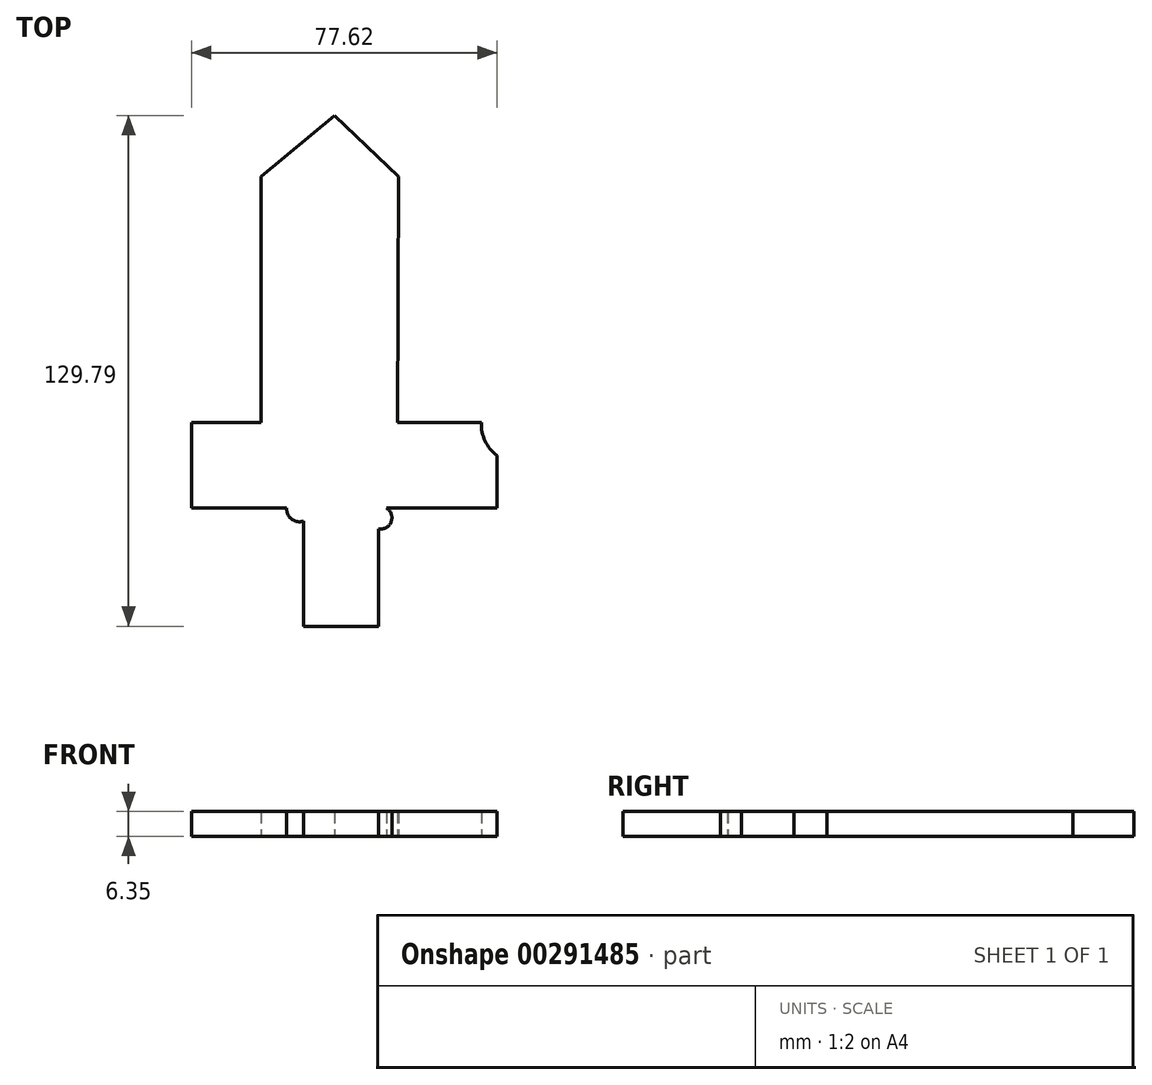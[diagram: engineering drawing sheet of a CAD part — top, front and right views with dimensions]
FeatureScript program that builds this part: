
annotation { "Feature Type Name" : "Feature", "Feature Type Description" : "" }
export const myFeature = defineFeature(function(context is Context, id is Id, definition is map)
    precondition{}
    {
        {
            var Q0;
            Q0=qCreatedBy(makeId("Top.planeOp"),FACE);
            var sketch = newSketch(context, id + "F0", { "sketchPlane" : qUnion([Q0])});
            skLineSegment(sketch, "E0", {"start": v(-7.85, -13.36) * mm, "end": v(-7.87, -43.45) * mm});
            skLineSegment(sketch, "E1", {"start": v(-7.87, -43.45) * mm, "end": v(11.29, -43.45) * mm});
            skLineSegment(sketch, "E2", {"start": v(11.29, -43.45) * mm, "end": v(11.29, -13.36) * mm});
            skLineSegment(sketch, "E3", {"start": v(11.29, -13.36) * mm, "end": v(41.34, -13.36) * mm});
            skLineSegment(sketch, "E4", {"start": v(41.34, 8.3) * mm, "end": v(37.36, 8.3) * mm});
            skLineSegment(sketch, "E5", {"start": v(-31.7, 8.3) * mm, "end": v(-36.28, 8.3) * mm});
            skLineSegment(sketch, "E6", {"start": v(-36.28, 8.3) * mm, "end": v(-36.28, -13.36) * mm});
            skLineSegment(sketch, "E7", {"start": v(-36.28, -13.36) * mm, "end": v(-7.85, -13.36) * mm});
            skLineSegment(sketch, "E8", {"start": v(37.36, 8.3) * mm, "end": v(41.34, 8.3) * mm});
            skLineSegment(sketch, "E9", {"start": v(41.34, 8.3) * mm, "end": v(41.34, -13.36) * mm});
            skArc(sketch, "E10", {"start": v(-32.06, -13.36) * mm, "mid": v(-33.58, -10.45) * mm, "end": v(-36.28, -8.58) * mm});
            skArc(sketch, "E11", {"start": v(-36.28, 4.36) * mm, "mid": v(-32.9, 5.07) * mm, "end": v(-31.7, 8.3) * mm});
            skArc(sketch, "E12", {"start": v(37.36, 8.3) * mm, "mid": v(38.29, 3.64) * mm, "end": v(41.34, 0) * mm});
            skArc(sketch, "E13", {"start": v(41.34, -8.02) * mm, "mid": v(38.64, -10.05) * mm, "end": v(37.97, -13.36) * mm});
            skArc(sketch, "E14", {"start": v(-12.1, -13.36) * mm, "mid": v(-10.88, -16.18) * mm, "end": v(-7.85, -16.73) * mm});
            skArc(sketch, "E15", {"start": v(11.29, -18.7) * mm, "mid": v(14.46, -16.83) * mm, "end": v(13.22, -13.36) * mm});
            skArc(sketch, "E16", {"start": v(11.29, -38.09) * mm, "mid": v(8.5, -40.33) * mm, "end": v(6.75, -43.45) * mm});
            skArc(sketch, "E17", {"start": v(-5.62, -43.45) * mm, "mid": v(-5.66, -40.95) * mm, "end": v(-7.87, -39.8) * mm});
            skLineSegment(sketch, "E18", {"start": v(-31.7, 8.3) * mm, "end": v(-27.14, 8.3) * mm});
            skPoint(sketch, "E19.end.orphan", {"position": v(-7.85, 8.3) * mm});
            skPoint(sketch, "E20.orphan", {"position": v(11.29, 8.3) * mm});
            skLineSegment(sketch, "E21", {"start": v(-27.14, 8.3) * mm, "end": v(-18.56, 8.3) * mm});
            skLineSegment(sketch, "E22", {"start": v(-18.56, 8.3) * mm, "end": v(-10.81, 8.3) * mm});
            skLineSegment(sketch, "E23", {"start": v(-10.81, 8.3) * mm, "end": v(-7.85, 8.3) * mm});
            skLineSegment(sketch, "E24", {"start": v(-2.81, 8.3) * mm, "end": v(-7.85, 8.3) * mm});
            skLineSegment(sketch, "E25", {"start": v(-2.81, 8.3) * mm, "end": v(4.78, 8.3) * mm});
            skLineSegment(sketch, "E26", {"start": v(4.78, 8.3) * mm, "end": v(14.34, 8.3) * mm});
            skLineSegment(sketch, "E27", {"start": v(14.34, 8.3) * mm, "end": v(17.81, 8.3) * mm});
            skLineSegment(sketch, "E28", {"start": v(17.81, 8.3) * mm, "end": v(31.78, 8.3) * mm});
            skLineSegment(sketch, "E29", {"start": v(31.78, 8.3) * mm, "end": v(37.36, 8.3) * mm});
            skLineSegment(sketch, "E30", {"start": v(-10.81, 44.3) * mm, "end": v(-10.84, 8.3) * mm});
            skLineSegment(sketch, "E31", {"start": v(-10.84, 8.3) * mm, "end": v(-10.81, 44.3) * mm});
            skPoint(sketch, "E32.end.orphan", {"position": v(-2.81, 51.89) * mm});
            skLineSegment(sketch, "E33", {"start": v(-10.81, 44.3) * mm, "end": v(-10.81, 66.33) * mm});
            skLineSegment(sketch, "E34", {"start": v(-10.81, 66.33) * mm, "end": v(0, 76.35) * mm});
            skLineSegment(sketch, "E35", {"start": v(0, 76.35) * mm, "end": v(11.36, 64.1) * mm});
            skLineSegment(sketch, "E36", {"start": v(11.36, 64.1) * mm, "end": v(11.29, 8.3) * mm});
            skLineSegment(sketch, "E37", {"start": v(-2.81, 8.3) * mm, "end": v(-2.81, 44.3) * mm});
            skLineSegment(sketch, "E38", {"start": v(-2.81, 44.3) * mm, "end": v(-2.81, 61.17) * mm});
            skLineSegment(sketch, "E39", {"start": v(-2.81, 61.17) * mm, "end": v(0, 65.1) * mm});
            skLineSegment(sketch, "E40", {"start": v(0, 65.1) * mm, "end": v(4.23, 62.08) * mm});
            skLineSegment(sketch, "E41", {"start": v(4.23, 62.08) * mm, "end": v(4.78, 8.3) * mm});
            skPoint(sketch, "E42.end.orphan", {"position": v(-6.43, 51.89) * mm});
            skArc(sketch, "E43", {"start": v(-7.85, 8.3) * mm, "mid": v(-7.8, 11.56) * mm, "end": v(-10.84, 12.77) * mm});
            skArc(sketch, "E44", {"start": v(11.3, 11.66) * mm, "mid": v(11.6, 9.96) * mm, "end": v(12.08, 8.3) * mm});
            skArc(sketch, "E45", {"start": v(11.3, 11.66) * mm, "mid": v(8.74, 10.86) * mm, "end": v(7.96, 8.3) * mm});
            skPoint(sketch, "E46.orphan", {"position": v(52.14, 13.7) * mm});
            skLineSegment(sketch, "E47", {"start": v(-2.81, 51.89) * mm, "end": v(-2.81, 61.17) * mm});
            skLineSegment(sketch, "E48", {"start": v(-7.85, 8.3) * mm, "end": v(-2.81, 8.3) * mm});
            skLineSegment(sketch, "E49", {"start": v(12.08, 8.3) * mm, "end": v(17.81, 8.3) * mm});
            skLineSegment(sketch, "E50", {"start": v(11.29, 8.3) * mm, "end": v(-7.85, 8.3) * mm});
            skLineSegment(sketch, "E51", {"start": v(11.29, 8.3) * mm, "end": v(11.32, 36.2) * mm});
            skLineSegment(sketch, "E52", {"start": v(11.32, 36.2) * mm, "end": v(11.29, 8.3) * mm});
            skLineSegment(sketch, "E53", {"start": v(-18.56, 8.3) * mm, "end": v(-18.56, 15.7) * mm});
            skLineSegment(sketch, "E54", {"start": v(-18.56, 70.78) * mm, "end": v(-18.56, 15.7) * mm});
            skLineSegment(sketch, "E55", {"start": v(-18.56, 70.78) * mm, "end": v(0, 86.34) * mm});
            skLineSegment(sketch, "E56", {"start": v(0, 86.34) * mm, "end": v(16.3, 70.78) * mm});
            skLineSegment(sketch, "E57", {"start": v(16.3, 70.78) * mm, "end": v(16.08, 8.3) * mm});
            skSolve(sketch);
        }
        {
            var Q0;
            {var subQ0=sQuery(id+"F0.wireOp",EDGE,"E26");Q0=makeQuery(id+"F0.imprint","IMPRINT",FACE,{"disambiguationData":[TD([[makeQuery(id+"F0.imprint","IMPRINT",EDGE,{"derivedFrom":subQ0}),1.0]])]});}
            var Q1;
            {var subQ0=sQuery(id+"F0.wireOp",EDGE,"E8");Q1=makeQuery(id+"F0.imprint","IMPRINT",FACE,{"disambiguationData":[TD([[makeQuery(id+"F0.imprint","IMPRINT",EDGE,{"derivedFrom":subQ0}),-1.0]])]});}
            var Q2;
            {var subQ1=sQuery(id+"F0.wireOp",EDGE,"E37");Q2=makeQuery(id+"F0.imprint","IMPRINT",FACE,{"disambiguationData":[TD([[makeQuery(id+"F0.imprint","IMPRINT",EDGE,{"derivedFrom":subQ1}),-1.0]])]});}
            var Q3;
            {var subQ3=sQuery(id+"F0.wireOp",EDGE,"E33");Q3=makeQuery(id+"F0.imprint","IMPRINT",FACE,{"disambiguationData":[TD([[makeQuery(id+"F0.imprint","IMPRINT",EDGE,{"derivedFrom":subQ3}),-1.0]])]});}
            var Q4;
            {var subQ3=sQuery(id+"F0.wireOp",EDGE,"E14");Q4=makeQuery(id+"F0.imprint","IMPRINT",FACE,{"disambiguationData":[TD([[makeQuery(id+"F0.imprint","IMPRINT",EDGE,{"derivedFrom":subQ3}),1.0]])]});}
            var Q5;
            {var subQ3=sQuery(id+"F0.wireOp",EDGE,"E16");Q5=makeQuery(id+"F0.imprint","IMPRINT",FACE,{"disambiguationData":[TD([[makeQuery(id+"F0.imprint","IMPRINT",EDGE,{"derivedFrom":subQ3}),1.0]])]});}
            var Q6;
            {var subQ3=sQuery(id+"F0.wireOp",EDGE,"E15");Q6=makeQuery(id+"F0.imprint","IMPRINT",FACE,{"disambiguationData":[TD([[makeQuery(id+"F0.imprint","IMPRINT",EDGE,{"derivedFrom":subQ3}),1.0]])]});}
            var Q7;
            {var subQ3=sQuery(id+"F0.wireOp",EDGE,"E13");Q7=makeQuery(id+"F0.imprint","IMPRINT",FACE,{"disambiguationData":[TD([[makeQuery(id+"F0.imprint","IMPRINT",EDGE,{"derivedFrom":subQ3}),1.0]])]});}
            var Q8;
            {var subQ0=sQuery(id+"F0.wireOp",EDGE,"E23");Q8=makeQuery(id+"F0.imprint","IMPRINT",FACE,{"disambiguationData":[TD([[makeQuery(id+"F0.imprint","IMPRINT",EDGE,{"derivedFrom":subQ0}),1.0]])]});}
            var Q9;
            {var subQ3=sQuery(id+"F0.wireOp",EDGE,"E17");Q9=makeQuery(id+"F0.imprint","IMPRINT",FACE,{"disambiguationData":[TD([[makeQuery(id+"F0.imprint","IMPRINT",EDGE,{"derivedFrom":subQ3}),1.0]])]});}
            var Q10;
            {var subQ0=sQuery(id+"F0.wireOp",EDGE,"E45");Q10=makeQuery(id+"F0.imprint","IMPRINT",FACE,{"disambiguationData":[TD([[makeQuery(id+"F0.imprint","IMPRINT",EDGE,{"derivedFrom":subQ0}),1.0]])]});}
            var Q11;
            {var subQ22=sQuery(id+"F0.wireOp",EDGE,"E10");Q11=makeQuery(id+"F0.imprint","IMPRINT",FACE,{"disambiguationData":[TD([[makeQuery(id+"F0.imprint","IMPRINT",EDGE,{"derivedFrom":subQ22}),-1.0]])]});}
            var Q12;
            {var subQ10=sQuery(id+"F0.wireOp",EDGE,"E33");Q12=makeQuery(id+"F0.imprint","IMPRINT",FACE,{"disambiguationData":[TD([[makeQuery(id+"F0.imprint","IMPRINT",EDGE,{"derivedFrom":subQ10}),1.0]])]});}
            var Q13;
            {var subQ0=sQuery(id+"F0.wireOp",EDGE,"E5");Q13=makeQuery(id+"F0.imprint","IMPRINT",FACE,{"disambiguationData":[TD([[makeQuery(id+"F0.imprint","IMPRINT",EDGE,{"derivedFrom":subQ0}),1.0]])]});}
            var Q14;
            {var subQ3=sQuery(id+"F0.wireOp",EDGE,"E10");Q14=makeQuery(id+"F0.imprint","IMPRINT",FACE,{"disambiguationData":[TD([[makeQuery(id+"F0.imprint","IMPRINT",EDGE,{"derivedFrom":subQ3}),1.0]])]});}
            extrude(context, id + "F1", {"entities" : qUnion([Q0, Q1, Q2, Q3, Q4, Q5, Q6, Q7, Q8, Q9, Q10, Q11, Q12, Q13, Q14]), "depth" : 6.35 * mm});
        }
    });
